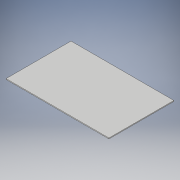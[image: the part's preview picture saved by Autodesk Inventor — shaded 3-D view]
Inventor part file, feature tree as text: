
AUTODESK INVENTOR PART (.ipt)
format: ipt  version: 2018 (Build 220112000, 112)  size: 90,112 bytes
history: native  units: in
note: dims shown in document units (in); Inventor stores cm internally (conversion verified against a paired STEP export)
features: extrude x1, sketch x1
ambient origin geometry x8: Origin, YZ Plane, XZ Plane, XY Plane, X Axis, Y Axis, Z Axis, Center Point
bodies: Solid1 (feature_tree)
feature tree (2):
  extrude  "Extrusion1"  Depth=2.3622in
  sketch  "Sketch1"  dims[d0=3.7402in d1=2.3622in d2=0.031in d3=0.0in]
